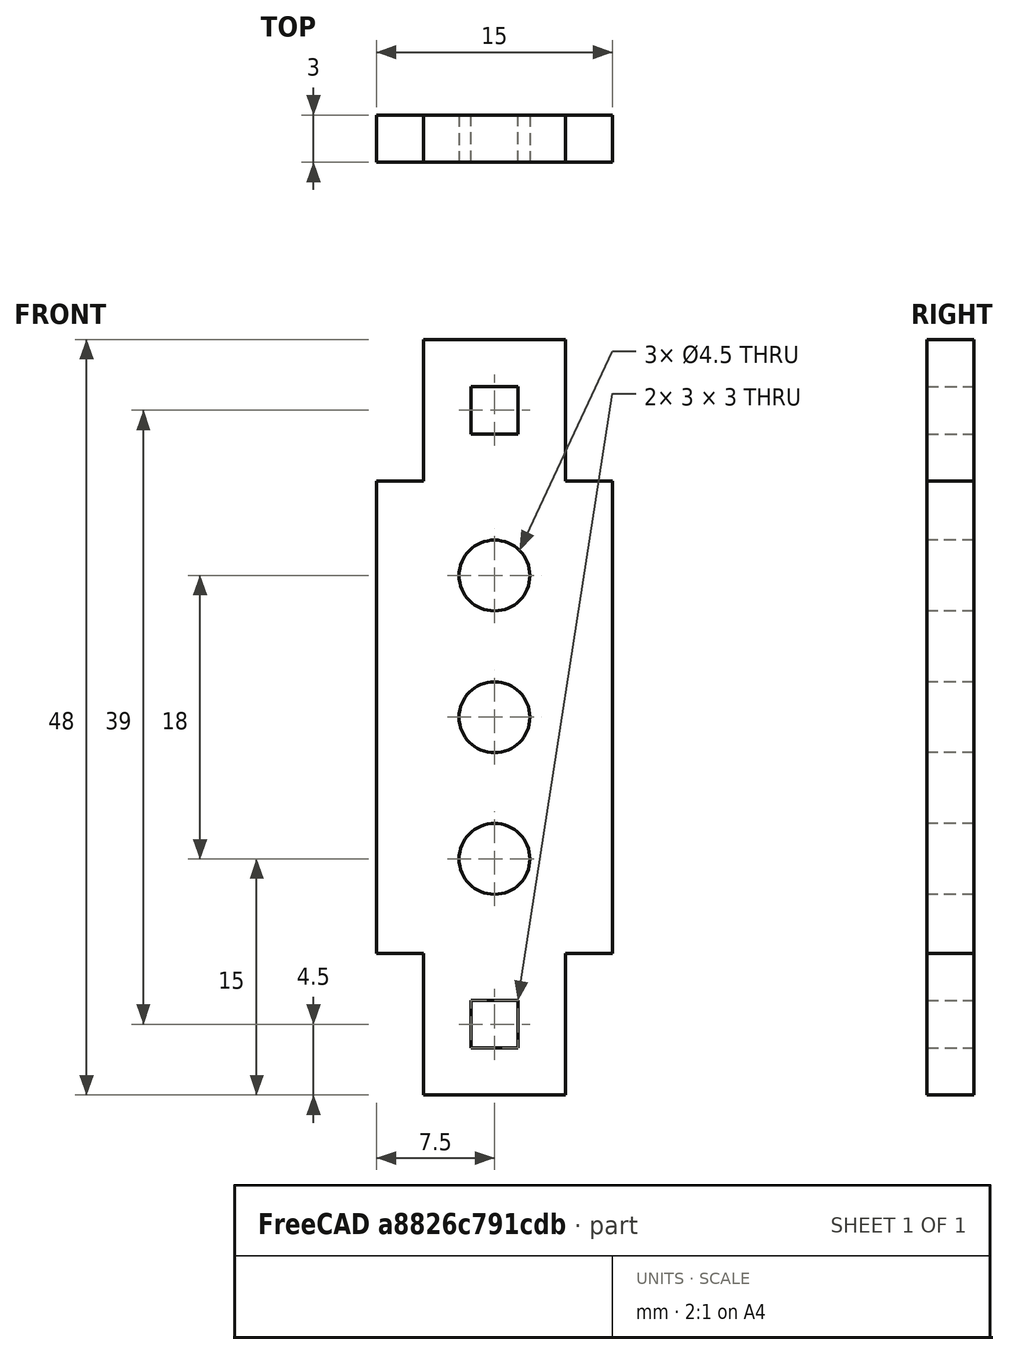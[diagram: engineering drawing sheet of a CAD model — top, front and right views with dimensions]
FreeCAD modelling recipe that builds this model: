
FCSTD DOCUMENT  (FreeCAD 0.16R6707 (Git))
Label: turretPitchRingConnector30
License: All rights reserved
LicenseURL: http://en.wikipedia.org/wiki/All_rights_reserved
objects: Part::Box×5, Part::Cut×5, Part::Cylinder×3, Part::MultiFuse×1
note: 14 computed .brp shape members not serialized (recipe doc carries the construction recipe); baked Part::Feature solids carry a one-line shape summary decoded from their .brp

FEATURE [Part::Box] Box009  label="Cube009"
  Height = 9
  Length = 9
  Placement = pos=(-4.5,-66,3) rot=(0,0,1;0rad)
  Width = 3
FEATURE [Part::Box] Box010  label="Cube010"
  Height = 3
  Length = 3
  Placement = pos=(-1.5,-66,6) rot=(0,0,1;0rad)
  Width = 3
FEATURE [Part::Cut] Cut010
  Base = -> Box009
  Tool = -> Box010
FEATURE [Part::Box] Box011  label="Cube011"
  Height = 30
  Length = 15
  Placement = pos=(-7.5,-66,-27) rot=(0,0,1;0rad)
  Width = 3
FEATURE [Part::Box] Box012  label="Cube012"
  Height = 9
  Length = 9
  Placement = pos=(-4.5,-66,3) rot=(0,0,1;0rad)
  Width = 3
FEATURE [Part::Box] Box013  label="Cube013"
  Height = 3
  Length = 3
  Placement = pos=(-1.5,-66,6) rot=(0,0,1;0rad)
  Width = 3
FEATURE [Part::Cut] Cut011
  Base = -> Box012
  Placement = pos=(0,0,-39) rot=(0,0,1;0rad)
  Tool = -> Box013
FEATURE [Part::MultiFuse] Fusion
  Shapes = -> [Cut011,Box011,Cut010]
FEATURE [Part::Cylinder] Cylinder004
  Angle = 360
  Height = 3
  Placement = pos=(0,-63,-12) rot=(1,0,0;1.5708rad)
  Radius = 2.25
FEATURE [Part::Cylinder] Cylinder005
  Angle = 360
  Height = 3
  Placement = pos=(0,-63,-3) rot=(1,0,0;1.5708rad)
  Radius = 2.25
FEATURE [Part::Cylinder] Cylinder006
  Angle = 360
  Height = 3
  Placement = pos=(0,-63,-21) rot=(1,0,0;1.5708rad)
  Radius = 2.25
FEATURE [Part::Cut] Cut012
  Base = -> Fusion
  Tool = -> Cylinder004
FEATURE [Part::Cut] Cut013
  Base = -> Cut012
  Tool = -> Cylinder006
FEATURE [Part::Cut] Cut014  label="pitchRingConnector"
  Base = -> Cut013
  Placement = pos=(0,29,-3) rot=(0,0,1;0rad)
  Tool = -> Cylinder005
